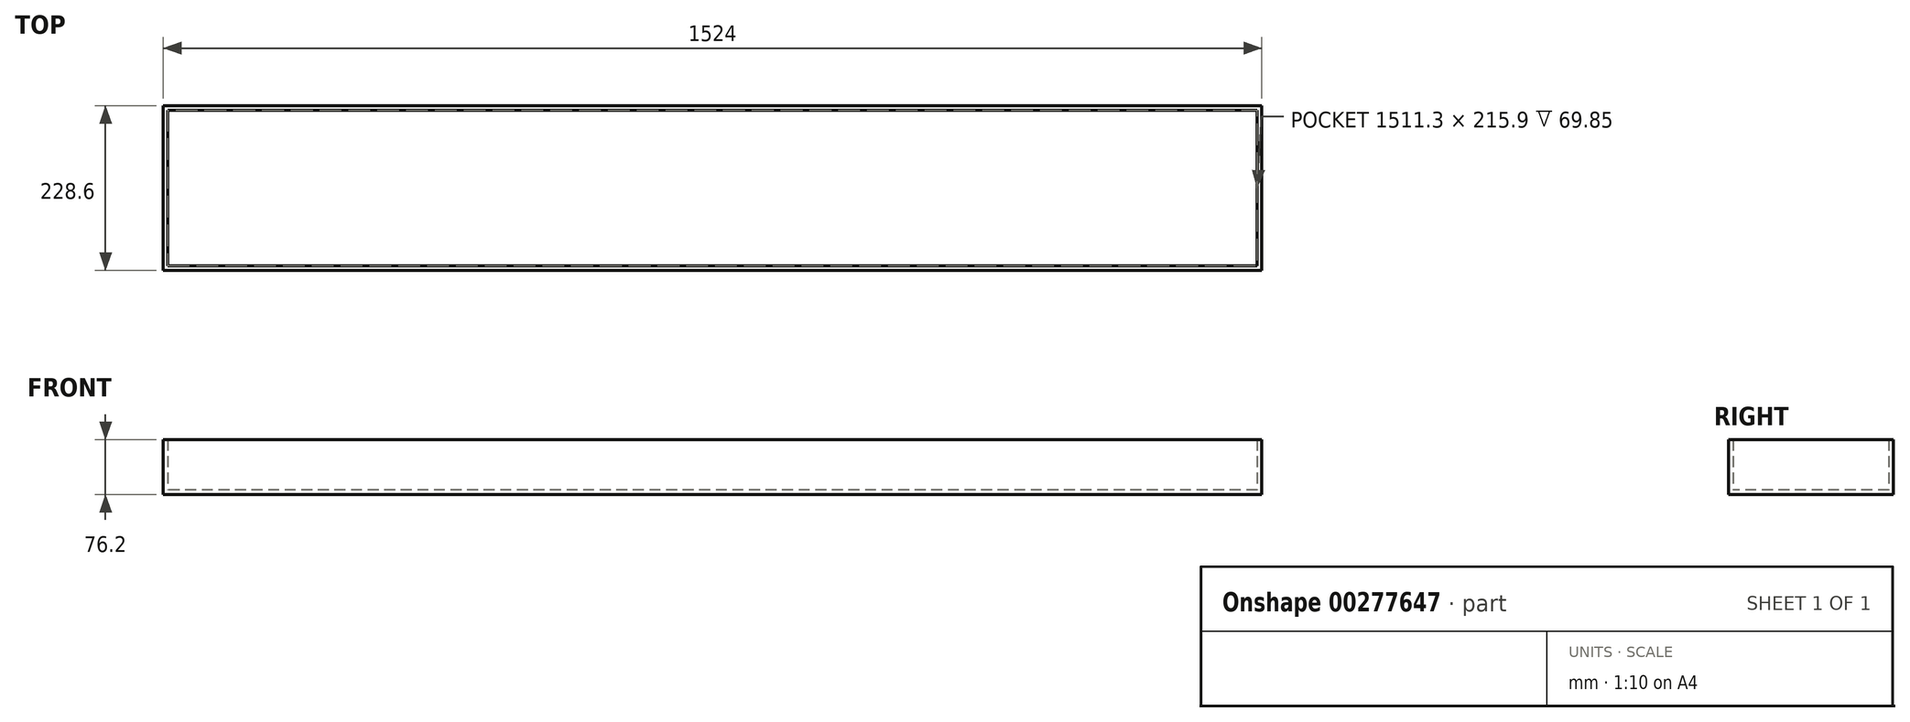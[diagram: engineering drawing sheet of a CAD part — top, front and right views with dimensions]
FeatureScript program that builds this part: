
annotation { "Feature Type Name" : "Feature", "Feature Type Description" : "" }
export const myFeature = defineFeature(function(context is Context, id is Id, definition is map)
    precondition{}
    {
        {
            var Q0;
            Q0=qCreatedBy(makeId("Top.planeOp"),FACE);
            var sketch = newSketch(context, id + "F0", { "sketchPlane" : qUnion([Q0])});
            skLineSegment(sketch, "E0.bottom", {"start": v(762, 114.3) * mm, "end": v(-762, 114.3) * mm});
            skLineSegment(sketch, "E0.top", {"start": v(762, -114.3) * mm, "end": v(-762, -114.3) * mm});
            skLineSegment(sketch, "E0.left", {"start": v(762, 114.3) * mm, "end": v(762, -114.3) * mm});
            skLineSegment(sketch, "E0.right", {"start": v(-762, 114.3) * mm, "end": v(-762, -114.3) * mm});
            skPoint(sketch, "E0.middle", {"position": v(0, 0) * mm});
            skSolve(sketch);
        }
        {
            var Q0;
            Q0 = qSketchRegion(id + "F0", true);
            extrude(context, id + "F1", {"entities" : qUnion([Q0]), "endBound" : BoundingType.SYMMETRIC, "depth" : 76.2 * mm});
        }
        {
            var Q0;
            Q0=makeQuery(id+"F1.opExtrude","CAP_FACE",FACE,{"disambiguationData":[OSD([sQuery(id+"F0.wireOp",EDGE,"E0.bottom"),sQuery(id+"F0.wireOp",EDGE,"E0.top"),sQuery(id+"F0.wireOp",EDGE,"E0.left"),sQuery(id+"F0.wireOp",EDGE,"E0.right")])],"isStart":false});
            shell(context, id + "F2", {"entities" : qUnion([Q0]), "thickness" : 6.35 * mm});
        }
    });
